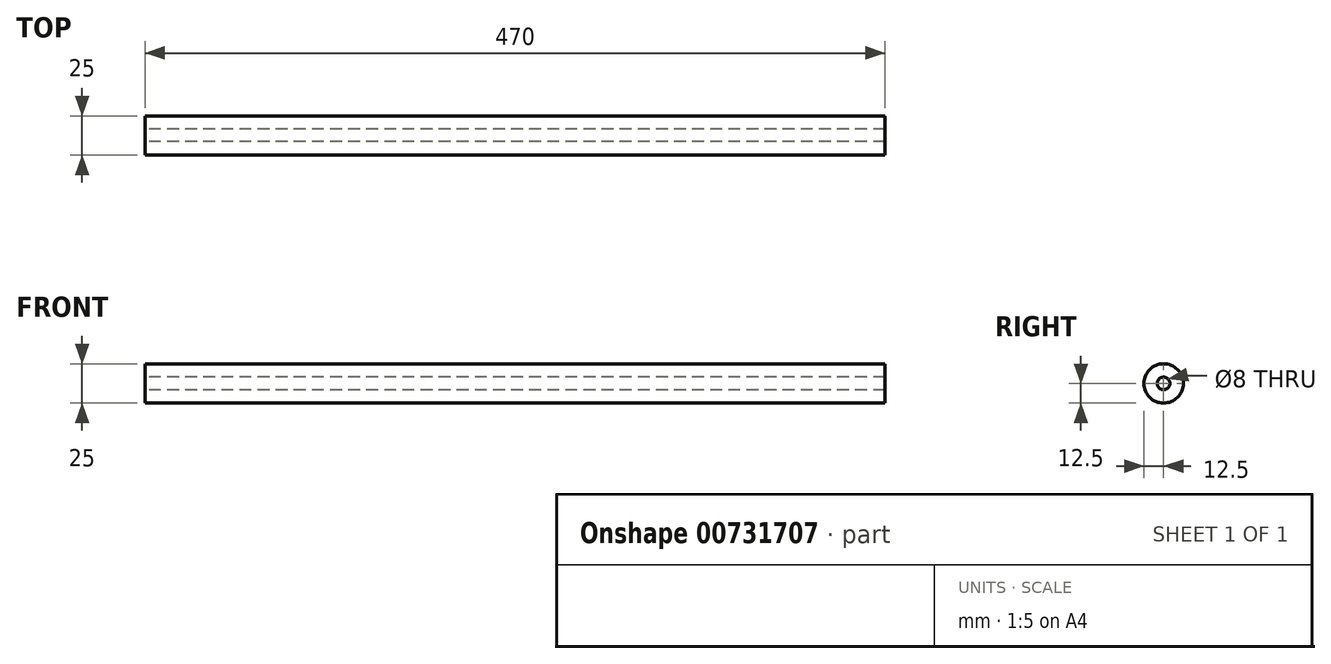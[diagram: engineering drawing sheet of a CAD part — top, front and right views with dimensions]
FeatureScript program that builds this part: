
annotation { "Feature Type Name" : "Feature", "Feature Type Description" : "" }
export const myFeature = defineFeature(function(context is Context, id is Id, definition is map)
    precondition{}
    {
        {
            var Q0;
            Q0=qCreatedBy(makeId("Right.planeOp"),FACE);
            var sketch = newSketch(context, id + "F0", { "sketchPlane" : qUnion([Q0])});
            skCircle(sketch, "E0", {"center": v(0, 0) * mm, "radius": 4 * mm});
            skCircle(sketch, "E1", {"center": v(0, 0) * mm, "radius": 12.5 * mm});
            skSolve(sketch);
        }
        {
            var Q0;
            Q0=makeQuery(id+"F0.imprint","IMPRINT",FACE,{"disambiguationData":[TD([[makeQuery(id+"F0.imprint","IMPRINT",EDGE,{"derivedFrom":sQuery(id+"F0.wireOp",EDGE,"E0")}),-1.0]])]});
            extrude(context, id + "F1", {"entities" : qUnion([Q0]), "depth" : 470 * mm, "offsetDistance" : 25 * mm, "symmetric" : true});
        }
    });
